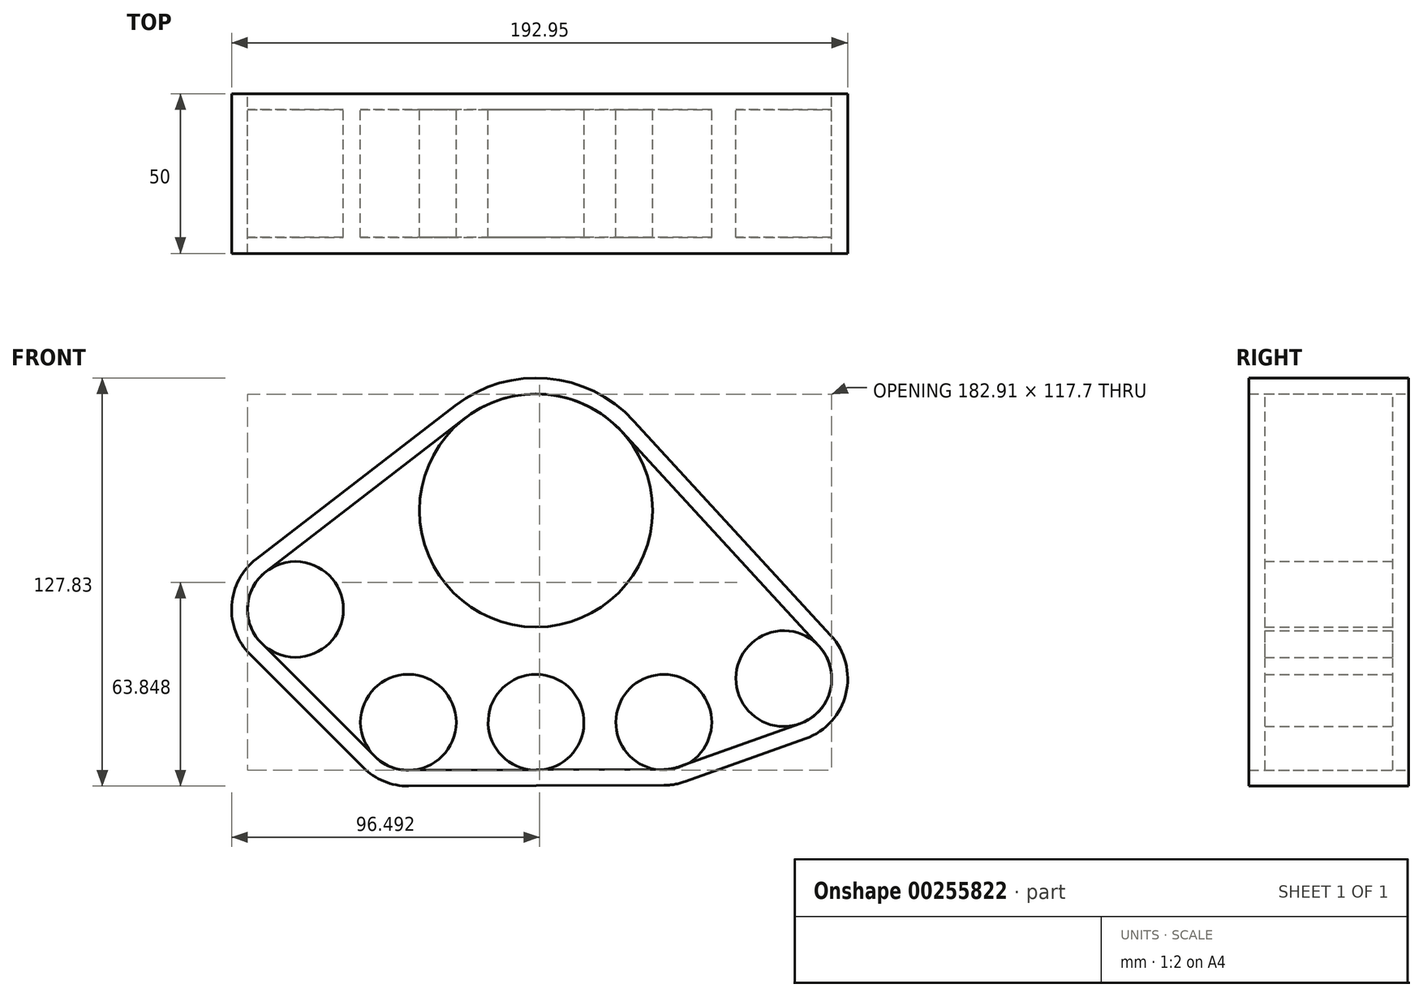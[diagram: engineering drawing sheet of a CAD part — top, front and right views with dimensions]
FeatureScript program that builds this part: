
annotation { "Feature Type Name" : "Feature", "Feature Type Description" : "" }
export const myFeature = defineFeature(function(context is Context, id is Id, definition is map)
    precondition{}
    {
        {
            var Q0;
            Q0=qCreatedBy(makeId("Front.planeOp"),FACE);
            var sketch = newSketch(context, id + "F0", { "sketchPlane" : qUnion([Q0])});
            skCircle(sketch, "E0", {"center": v(0, 0) * mm, "radius": 36.5 * mm});
            skCircle(sketch, "E1", {"center": v(-75.36, -30.98) * mm, "radius": 15 * mm});
            skCircle(sketch, "E2", {"center": v(-40, -66.33) * mm, "radius": 15 * mm});
            skCircle(sketch, "E3", {"center": v(40, -66.33) * mm, "radius": 15 * mm});
            skCircle(sketch, "E4", {"center": v(0, -66.33) * mm, "radius": 15 * mm});
            skCircle(sketch, "E5", {"center": v(77.59, -52.65) * mm, "radius": 15 * mm});
            skLineSegment(sketch, "E6", {"start": v(77.59, -52.65) * mm, "end": v(40, -66.33) * mm, "construction": true});
            skLineSegment(sketch, "E7", {"start": v(-40, -66.33) * mm, "end": v(-75.36, -30.98) * mm, "construction": true});
            skSolve(sketch);
        }
        {
            var Q0;
            Q0=makeQuery(id+"F0.imprint","IMPRINT",FACE,{"disambiguationData":[TD([[makeQuery(id+"F0.imprint","IMPRINT",EDGE,{"derivedFrom":sQuery(id+"F0.wireOp",EDGE,"E0")}),1.0]])]});
            var Q1;
            Q1=makeQuery(id+"F0.imprint","IMPRINT",FACE,{"disambiguationData":[TD([[makeQuery(id+"F0.imprint","IMPRINT",EDGE,{"derivedFrom":sQuery(id+"F0.wireOp",EDGE,"E2")}),1.0]])]});
            var Q2;
            Q2=makeQuery(id+"F0.imprint","IMPRINT",FACE,{"disambiguationData":[TD([[makeQuery(id+"F0.imprint","IMPRINT",EDGE,{"derivedFrom":sQuery(id+"F0.wireOp",EDGE,"E1")}),1.0]])]});
            var Q3;
            Q3=makeQuery(id+"F0.imprint","IMPRINT",FACE,{"disambiguationData":[TD([[makeQuery(id+"F0.imprint","IMPRINT",EDGE,{"derivedFrom":sQuery(id+"F0.wireOp",EDGE,"E3")}),1.0]])]});
            var Q4;
            Q4=makeQuery(id+"F0.imprint","IMPRINT",FACE,{"disambiguationData":[TD([[makeQuery(id+"F0.imprint","IMPRINT",EDGE,{"derivedFrom":sQuery(id+"F0.wireOp",EDGE,"E5")}),1.0]])]});
            var Q5;
            Q5=makeQuery(id+"F0.imprint","IMPRINT",FACE,{"disambiguationData":[TD([[makeQuery(id+"F0.imprint","IMPRINT",EDGE,{"derivedFrom":sQuery(id+"F0.wireOp",EDGE,"E4")}),1.0]])]});
            extrude(context, id + "F1", {"entities" : qUnion([Q0, Q1, Q2, Q3, Q4, Q5]), "depth" : 40 * mm});
        }
        {
            var Q0;
            Q0=qCreatedBy(makeId("Front.planeOp"),FACE);
            cPlane(context, id + "F2", {"entities" : qUnion([Q0]), "cplaneType" : CPlaneType.OFFSET, "offset" : 5 * mm, "oppositeDirection" : true, "width" : 150 * mm, "height" : 150 * mm});
        }
        {
            var Q0;
            Q0=qCreatedBy(id+"F2.planeOp",FACE);
            var sketch = newSketch(context, id + "F3", { "sketchPlane" : qUnion([Q0])});
            skCircle(sketch, "E8.0.0", {"center": v(0, 0) * mm, "radius": 36.5 * mm, "construction": true});
            skCircle(sketch, "E9.0.0", {"center": v(-75.36, -30.98) * mm, "radius": 15 * mm, "construction": true});
            skCircle(sketch, "E10.0.0", {"center": v(-40, -66.33) * mm, "radius": 15 * mm, "construction": true});
            skCircle(sketch, "E11.0.0", {"center": v(0, -66.33) * mm, "radius": 15 * mm, "construction": true});
            skCircle(sketch, "E12.0.0", {"center": v(40, -66.33) * mm, "radius": 15 * mm, "construction": true});
            skCircle(sketch, "E13.0.0", {"center": v(77.59, -52.65) * mm, "radius": 15 * mm, "construction": true});
            skArc(sketch, "E14.0", {"start": v(30.56, 28.08) * mm, "mid": v(3.53, 41.35) * mm, "end": v(-25.35, 32.86) * mm});
            skArc(sketch, "E15.0", {"start": v(-87.57, -15.14) * mm, "mid": v(-95.31, -29.7) * mm, "end": v(-89.5, -45.12) * mm});
            skArc(sketch, "E16.0", {"start": v(-54.14, -80.47) * mm, "mid": v(-47.62, -84.82) * mm, "end": v(-39.94, -86.33) * mm});
            skArc(sketch, "E17.0", {"start": v(84.43, -71.44) * mm, "mid": v(97.02, -57.39) * mm, "end": v(92.31, -39.12) * mm});
            skLineSegment(sketch, "E18", {"start": v(-87.57, -15.14) * mm, "end": v(-25.35, 32.86) * mm});
            skLineSegment(sketch, "E19", {"start": v(30.56, 28.08) * mm, "end": v(92.31, -39.12) * mm});
            skLineSegment(sketch, "E20", {"start": v(0, -86.2) * mm, "end": v(-39.94, -86.33) * mm});
            skLineSegment(sketch, "E21", {"start": v(-54.14, -80.47) * mm, "end": v(-89.5, -45.12) * mm});
            skArc(sketch, "E22", {"start": v(40.06, -86.08) * mm, "mid": v(43.4, -85.78) * mm, "end": v(46.64, -84.93) * mm});
            skLineSegment(sketch, "E23", {"start": v(84.43, -71.44) * mm, "end": v(46.64, -84.93) * mm});
            skLineSegment(sketch, "E24", {"start": v(0, -86.2) * mm, "end": v(40.06, -86.08) * mm});
            skSolve(sketch);
        }
        {
            var Q0;
            Q0=makeQuery(id+"F3.imprint","IMPRINT",FACE,{"disambiguationData":[TD([[makeQuery(id+"F3.imprint","IMPRINT",EDGE,{"derivedFrom":sQuery(id+"F3.wireOp",EDGE,"E14.0")}),1.0]])]});
            extrude(context, id + "F4", {"entities" : qUnion([Q0]), "depth" : 50 * mm});
        }
        {
            var Q0;
            Q0=makeQuery(id+"F4.opExtrude","CAP_FACE",FACE,{"disambiguationData":[OSD([sQuery(id+"F3.wireOp",EDGE,"E14.0"),sQuery(id+"F3.wireOp",EDGE,"E15.0"),sQuery(id+"F3.wireOp",EDGE,"E16.0"),sQuery(id+"F3.wireOp",EDGE,"E17.0"),sQuery(id+"F3.wireOp",EDGE,"E18"),sQuery(id+"F3.wireOp",EDGE,"E19"),sQuery(id+"F3.wireOp",EDGE,"E20"),sQuery(id+"F3.wireOp",EDGE,"E21"),sQuery(id+"F3.wireOp",EDGE,"E22"),sQuery(id+"F3.wireOp",EDGE,"E23"),sQuery(id+"F3.wireOp",EDGE,"E24")])],"isStart":false});
            var Q1;
            Q1=makeQuery(id+"F4.opExtrude","CAP_FACE",FACE,{"disambiguationData":[OSD([sQuery(id+"F3.wireOp",EDGE,"E14.0"),sQuery(id+"F3.wireOp",EDGE,"E15.0"),sQuery(id+"F3.wireOp",EDGE,"E16.0"),sQuery(id+"F3.wireOp",EDGE,"E17.0"),sQuery(id+"F3.wireOp",EDGE,"E18"),sQuery(id+"F3.wireOp",EDGE,"E19"),sQuery(id+"F3.wireOp",EDGE,"E20"),sQuery(id+"F3.wireOp",EDGE,"E21"),sQuery(id+"F3.wireOp",EDGE,"E22"),sQuery(id+"F3.wireOp",EDGE,"E23"),sQuery(id+"F3.wireOp",EDGE,"E24")])],"isStart":true});
            shell(context, id + "F5", {"entities" : qUnion([Q0, Q1]), "thickness" : 5 * mm});
        }
    });
